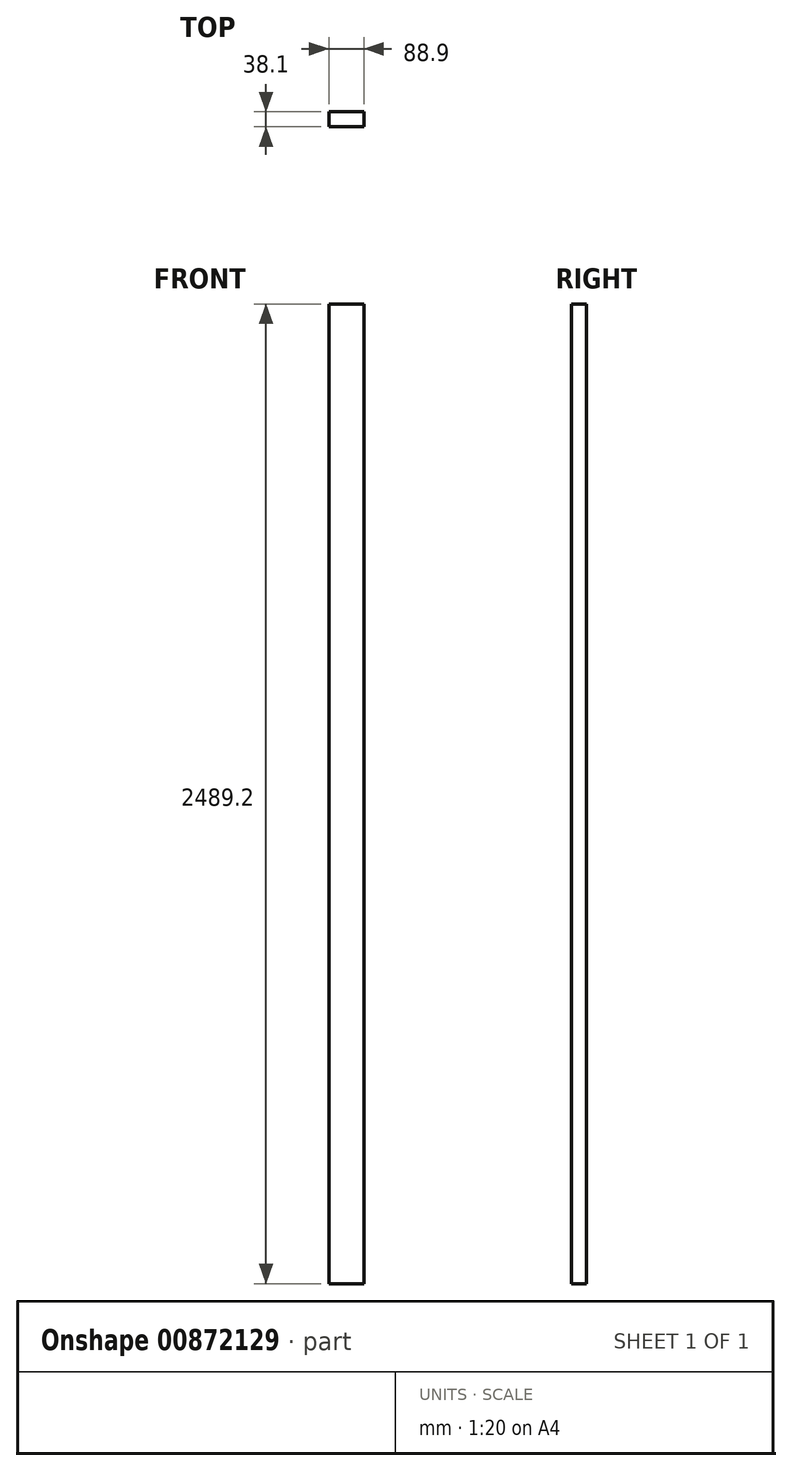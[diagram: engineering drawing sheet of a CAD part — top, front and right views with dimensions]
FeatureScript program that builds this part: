
annotation { "Feature Type Name" : "Feature", "Feature Type Description" : "" }
export const myFeature = defineFeature(function(context is Context, id is Id, definition is map)
    precondition{}
    {
        {
            var Q0;
            Q0=qCreatedBy(makeId("Front.planeOp"),FACE);
            var sketch = newSketch(context, id + "F0", { "sketchPlane" : qUnion([Q0])});
            skLineSegment(sketch, "E0.bottom", {"start": v(0, 0) * mm, "end": v(88.9, 0) * mm});
            skLineSegment(sketch, "E0.top", {"start": v(0, 2489.2) * mm, "end": v(88.9, 2489.2) * mm});
            skLineSegment(sketch, "E0.left", {"start": v(0, 0) * mm, "end": v(0, 2489.2) * mm});
            skLineSegment(sketch, "E0.right", {"start": v(88.9, 0) * mm, "end": v(88.9, 2489.2) * mm});
            skSolve(sketch);
        }
        {
            var Q0;
            Q0=makeQuery(id+"F0.imprint","IMPRINT",FACE,{"disambiguationData":[TD([[makeQuery(id+"F0.imprint","IMPRINT",EDGE,{"derivedFrom":sQuery(id+"F0.wireOp",EDGE,"E0.bottom")}),1.0]])]});
            extrude(context, id + "F1", {"entities" : qUnion([Q0]), "depth" : 38.1 * mm, "offsetDistance" : 25.4 * mm});
        }
    });
